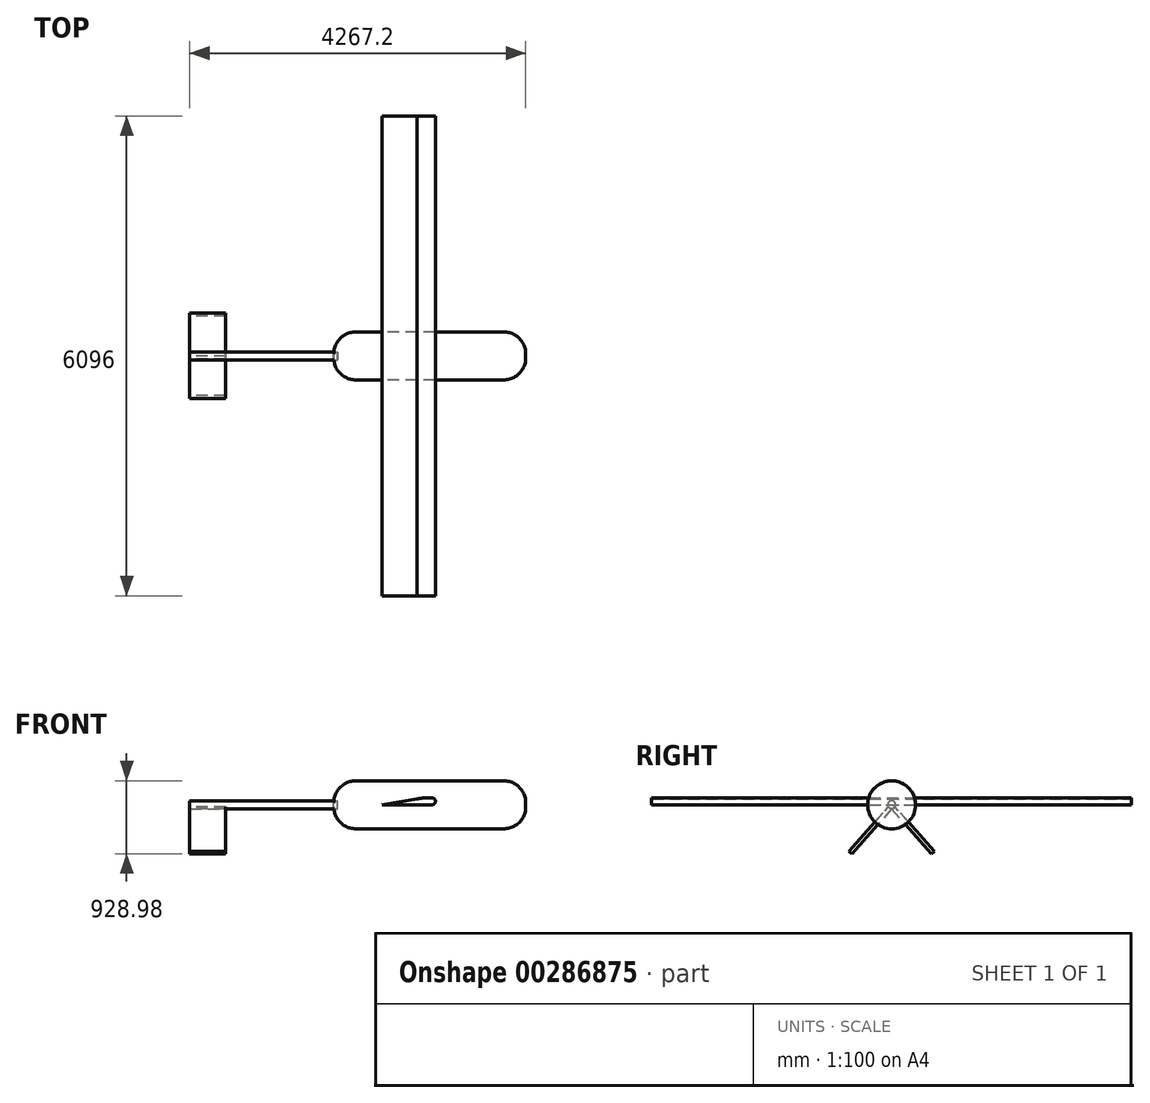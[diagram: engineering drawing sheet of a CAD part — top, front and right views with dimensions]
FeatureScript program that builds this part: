
annotation { "Feature Type Name" : "Feature", "Feature Type Description" : "" }
export const myFeature = defineFeature(function(context is Context, id is Id, definition is map)
    precondition{}
    {
        {
            var Q0;
            Q0=qCreatedBy(makeId("Right.planeOp"),FACE);
            var sketch = newSketch(context, id + "F0", { "sketchPlane" : qUnion([Q0])});
            skCircle(sketch, "E0", {"center": v(0, 0) * mm, "radius": 304.8 * mm});
            skSolve(sketch);
        }
        {
            var Q0;
            Q0=makeQuery(id+"F0.imprint","IMPRINT",FACE,{"disambiguationData":[TD([[makeQuery(id+"F0.imprint","IMPRINT",EDGE,{"derivedFrom":sQuery(id+"F0.wireOp",EDGE,"E0")}),1.0]])]});
            extrude(context, id + "F1", {"entities" : qUnion([Q0]), "depth" : 2438.4 * mm});
        }
        {
            var Q0;
            Q0=makeQuery(id+"F1.opExtrude","CAP_EDGE",EDGE,{"disambiguationData":[OSD([sQuery(id+"F0.wireOp",EDGE,"E0")])],"isStart":false});
            var Q1;
            Q1=makeQuery(id+"F1.opExtrude","CAP_EDGE",EDGE,{"disambiguationData":[OSD([sQuery(id+"F0.wireOp",EDGE,"E0")])],"isStart":true});
            fillet(context, id + "F2", {"entities" : qUnion([Q0, Q1]), "radius" : 279.4 * mm, "tangentPropagation" : true, "allowEdgeOverflow" : false});
        }
        {
            var Q0;
            Q0=qCreatedBy(makeId("Front.planeOp"),FACE);
            var sketch = newSketch(context, id + "F3", { "sketchPlane" : qUnion([Q0])});
            skLineSegment(sketch, "E1", {"start": v(615.47, 0) * mm, "end": v(1246.1, 0) * mm});
            skLineSegment(sketch, "E2", {"start": v(615.47, 0) * mm, "end": v(1056.91, 76.34) * mm});
            skArc(sketch, "E3", {"start": v(1246.1, 0) * mm, "mid": v(1290.9, 44.8) * mm, "end": v(1246.1, 89.62) * mm});
            skArc(sketch, "E4", {"start": v(1246.1, 89.62) * mm, "mid": v(1151.27, 86.3) * mm, "end": v(1056.91, 76.34) * mm});
            skSolve(sketch);
        }
        {
            var Q0;
            Q0 = qSketchRegion(id + "F3", true);
            var Q1;
            Q1=sQuery(id+"F3.wireOp",EDGE,"E2");
            var Q2;
            Q2=sQuery(id+"F3.wireOp",EDGE,"E4");
            var Q3;
            Q3=sQuery(id+"F3.wireOp",EDGE,"E3");
            var Q4;
            Q4=sQuery(id+"F3.wireOp",EDGE,"E1");
            extrude(context, id + "F4", {"entities" : qUnion([Q0]), "surfaceEntities" : qUnion([Q1, Q2, Q3, Q4]), "endBound" : BoundingType.SYMMETRIC, "depth" : 6096 * mm});
        }
        {
            var Q0;
            Q0=qCreatedBy(makeId("Right.planeOp"),FACE);
            var sketch = newSketch(context, id + "F5", { "sketchPlane" : qUnion([Q0])});
            skCircle(sketch, "E5", {"center": v(0, 0) * mm, "radius": 50.8 * mm});
            skSolve(sketch);
        }
        {
            var Q0;
            Q0 = qSketchRegion(id + "F5", true);
            var Q1;
            Q1=sQuery(id+"F5.wireOp",EDGE,"E5");
            extrude(context, id + "F6", {"entities" : qUnion([Q0]), "surfaceEntities" : qUnion([Q1]), "oppositeDirection" : true, "depth" : 1828.8 * mm, "hasSecondDirection" : true, "secondDirectionOppositeDirection" : false, "secondDirectionDepth" : 50.8 * mm});
        }
        {
            var Q0;
            Q0=qCreatedBy(makeId("Right.planeOp"),FACE);
            cPlane(context, id + "F7", {"entities" : qUnion([Q0]), "cplaneType" : CPlaneType.OFFSET, "offset" : 1828.8 * mm, "oppositeDirection" : true, "width" : 152.4 * mm, "height" : 152.4 * mm});
        }
        {
            var Q0;
            Q0=qCreatedBy(id+"F7.planeOp",FACE);
            var sketch = newSketch(context, id + "F8", { "sketchPlane" : qUnion([Q0])});
            skLineSegment(sketch, "E6", {"start": v(0, -54.65) * mm, "end": v(506.24, -624.18) * mm});
            skLineSegment(sketch, "E7", {"start": v(506.24, -624.18) * mm, "end": v(544.21, -590.43) * mm});
            skLineSegment(sketch, "E8", {"start": v(544.21, -590.43) * mm, "end": v(41.95, -25.38) * mm});
            skLineSegment(sketch, "E9", {"start": v(41.95, -25.38) * mm, "end": v(0, -54.65) * mm});
            skLineSegment(sketch, "E10.MirrorCS", {"start": v(-41.95, -25.38) * mm, "end": v(0, -54.65) * mm});
            skLineSegment(sketch, "E11.MirrorCS", {"start": v(-544.21, -590.43) * mm, "end": v(-41.95, -25.38) * mm});
            skLineSegment(sketch, "E12.MirrorCS", {"start": v(0, -54.65) * mm, "end": v(-506.24, -624.18) * mm});
            skLineSegment(sketch, "E13.MirrorCS", {"start": v(-506.24, -624.18) * mm, "end": v(-544.21, -590.43) * mm});
            skSolve(sketch);
        }
        {
            var Q0;
            Q0 = qSketchRegion(id + "F8", true);
            extrude(context, id + "F9", {"entities" : qUnion([Q0]), "depth" : 457.2 * mm});
        }
    });
